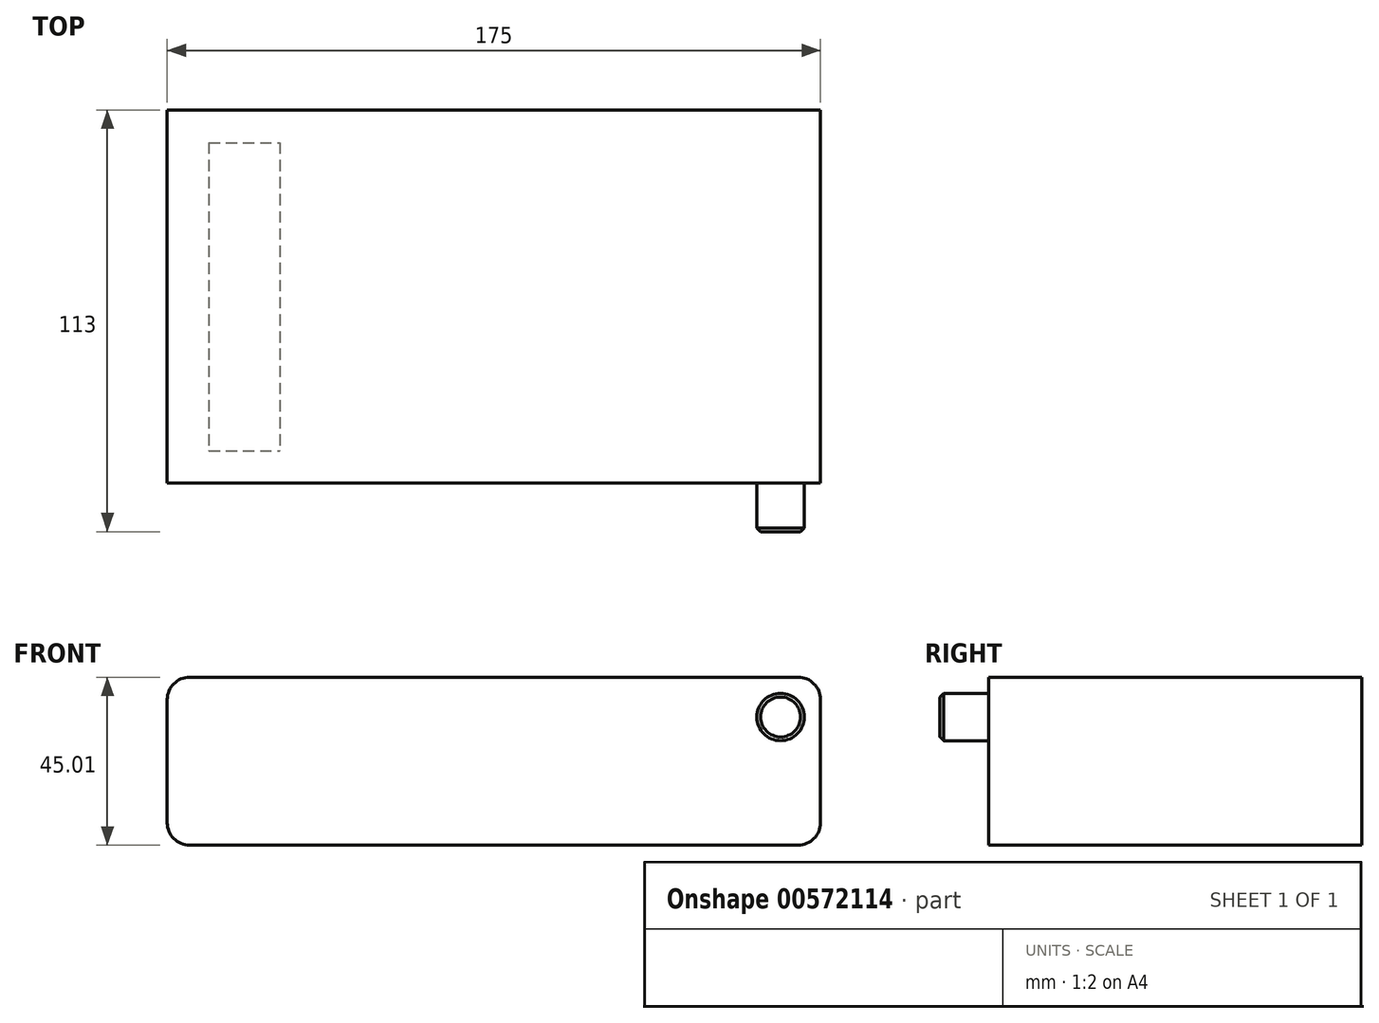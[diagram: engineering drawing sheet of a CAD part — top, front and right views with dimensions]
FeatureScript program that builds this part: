
annotation { "Feature Type Name" : "Feature", "Feature Type Description" : "" }
export const myFeature = defineFeature(function(context is Context, id is Id, definition is map)
    precondition{}
    {
        {
            var Q0;
            Q0=qCreatedBy(makeId("Top.planeOp"),FACE);
            var sketch = newSketch(context, id + "F0", { "sketchPlane" : qUnion([Q0])});
            skLineSegment(sketch, "E0.bottom", {"start": v(87.5, 50) * mm, "end": v(-87.5, 50) * mm});
            skLineSegment(sketch, "E0.top", {"start": v(87.5, -50) * mm, "end": v(-87.5, -50) * mm});
            skLineSegment(sketch, "E0.left", {"start": v(87.5, 50) * mm, "end": v(87.5, -50) * mm});
            skLineSegment(sketch, "E0.right", {"start": v(-87.5, 50) * mm, "end": v(-87.5, -50) * mm});
            skPoint(sketch, "E0.middle", {"position": v(0, 0) * mm});
            skSolve(sketch);
        }
        {
            var Q0;
            Q0=makeQuery(id+"F0.imprint","IMPRINT",FACE,{"disambiguationData":[TD([[makeQuery(id+"F0.imprint","IMPRINT",EDGE,{"derivedFrom":sQuery(id+"F0.wireOp",EDGE,"E0.bottom")}),1.0]])]});
            extrude(context, id + "F1", {"entities" : qUnion([Q0]), "depth" : 45 * mm, "offsetDistance" : 25.4 * mm});
        }
        {
            var Q0;
            Q0=makeQuery(id+"F1.opExtrude","SWEPT_FACE",FACE,{"disambiguationData":[OSD([sQuery(id+"F0.wireOp",EDGE,"E0.top")])]});
            var sketch = newSketch(context, id + "F2", { "sketchPlane" : qUnion([Q0])});
            skCircle(sketch, "E1", {"center": v(76.8, 34.36) * mm, "radius": 6.35 * mm});
            skSolve(sketch);
        }
        {
            var Q0;
            Q0=makeQuery(id+"F2.imprint","IMPRINT",FACE,{"disambiguationData":[TD([[makeQuery(id+"F2.imprint","IMPRINT",EDGE,{"derivedFrom":sQuery(id+"F2.wireOp",EDGE,"E1")}),1.0]])]});
            extrude(context, id + "F3", {"entities" : qUnion([Q0]), "operationType" : NewBodyOperationType.ADD, "depth" : 13 * mm, "offsetDistance" : 25.4 * mm});
        }
        {
            var Q0;
            Q0=makeQuery(id+"F3.opExtrude","CAP_EDGE",EDGE,{"disambiguationData":[OSD([sQuery(id+"F2.wireOp",EDGE,"E1")])],"isStart":false});
            chamfer(context, id + "F4", {"entities" : qUnion([Q0]), "width" : 1 * mm, "tangentPropagation" : true});
        }
        {
            var Q0;
            Q0=makeQuery(id+"F1.opExtrude","CAP_EDGE",EDGE,{"disambiguationData":[OSD([sQuery(id+"F0.wireOp",EDGE,"E0.right")])],"isStart":false});
            var Q1;
            Q1=makeQuery(id+"F1.opExtrude","CAP_EDGE",EDGE,{"disambiguationData":[OSD([sQuery(id+"F0.wireOp",EDGE,"E0.left")])],"isStart":false});
            var Q2;
            Q2=makeQuery(id+"F1.opExtrude","CAP_EDGE",EDGE,{"disambiguationData":[OSD([sQuery(id+"F0.wireOp",EDGE,"E0.left")])],"isStart":true});
            var Q3;
            Q3=makeQuery(id+"F1.opExtrude","CAP_EDGE",EDGE,{"disambiguationData":[OSD([sQuery(id+"F0.wireOp",EDGE,"E0.right")])],"isStart":true});
            fillet(context, id + "F5", {"entities" : qUnion([Q0, Q1, Q2, Q3]), "radius" : 6 * mm, "tangentPropagation" : true, "allowEdgeOverflow" : false});
        }
        {
            var Q0;
            Q0=makeQuery(id+"F1.opExtrude","CAP_FACE",FACE,{"disambiguationData":[OSD([sQuery(id+"F0.wireOp",EDGE,"E0.bottom"),sQuery(id+"F0.wireOp",EDGE,"E0.top"),sQuery(id+"F0.wireOp",EDGE,"E0.left"),sQuery(id+"F0.wireOp",EDGE,"E0.right")])],"isStart":true});
            var sketch = newSketch(context, id + "F6", { "sketchPlane" : qUnion([Q0])});
            skLineSegment(sketch, "E2.bottom", {"start": v(-76.39, -41.27) * mm, "end": v(-57.34, -41.27) * mm});
            skLineSegment(sketch, "E2.top", {"start": v(-76.39, 41.27) * mm, "end": v(-57.34, 41.27) * mm});
            skLineSegment(sketch, "E2.left", {"start": v(-76.39, -41.27) * mm, "end": v(-76.39, 41.27) * mm});
            skLineSegment(sketch, "E2.right", {"start": v(-57.34, -41.27) * mm, "end": v(-57.34, 41.27) * mm});
            skPoint(sketch, "E2.middle", {"position": v(-66.86, 0) * mm});
            skSolve(sketch);
        }
        {
            var Q0;
            Q0=makeQuery(id+"F6.imprint","IMPRINT",FACE,{"disambiguationData":[TD([[makeQuery(id+"F6.imprint","IMPRINT",EDGE,{"derivedFrom":sQuery(id+"F6.wireOp",EDGE,"E2.bottom")}),1.0]])]});
            extrude(context, id + "F7", {"entities" : qUnion([Q0]), "operationType" : NewBodyOperationType.ADD, "depth" : 1 / 406.4 * mm, "offsetDistance" : 25.4 * mm});
        }
        {
            var Q0;
            Q0=makeQuery(id+"F7.opExtrude","SWEPT_EDGE",EDGE,{"disambiguationData":[OSD([sQuery(id+"F6.wireOp",EDGE,"E2.top"),sQuery(id+"F6.wireOp",EDGE,"E2.left")])]});
            var Q1;
            Q1=makeQuery(id+"F7.opExtrude","SWEPT_EDGE",EDGE,{"disambiguationData":[OSD([sQuery(id+"F6.wireOp",EDGE,"E2.top"),sQuery(id+"F6.wireOp",EDGE,"E2.right")])]});
            var Q2;
            Q2=makeQuery(id+"F7.opExtrude","SWEPT_EDGE",EDGE,{"disambiguationData":[OSD([sQuery(id+"F6.wireOp",EDGE,"E2.bottom"),sQuery(id+"F6.wireOp",EDGE,"E2.left")])]});
            var Q3;
            Q3=makeQuery(id+"F7.opExtrude","SWEPT_EDGE",EDGE,{"disambiguationData":[OSD([sQuery(id+"F6.wireOp",EDGE,"E2.bottom"),sQuery(id+"F6.wireOp",EDGE,"E2.right")])]});
            fillet(context, id + "F8", {"entities" : qUnion([Q0, Q1, Q2, Q3]), "radius" : 3 / 203.2 * mm, "tangentPropagation" : true, "allowEdgeOverflow" : false});
        }
    });
